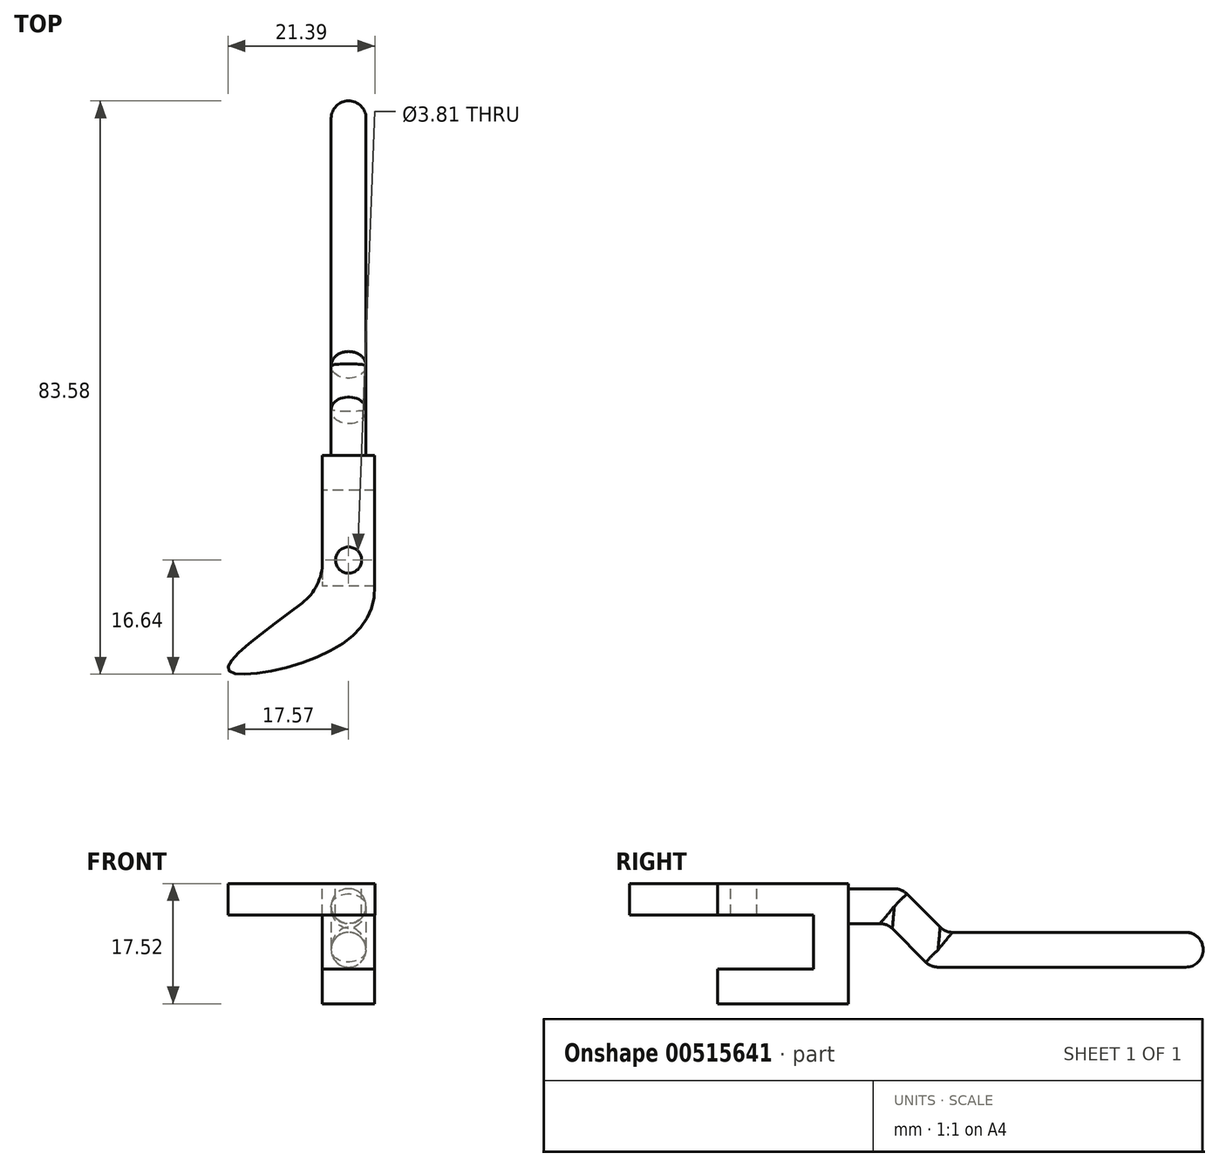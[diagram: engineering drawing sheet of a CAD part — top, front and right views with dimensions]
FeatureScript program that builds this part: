
annotation { "Feature Type Name" : "Feature", "Feature Type Description" : "" }
export const myFeature = defineFeature(function(context is Context, id is Id, definition is map)
    precondition{}
    {
        {
            var Q0;
            Q0=qCreatedBy(makeId("Top.planeOp"),FACE);
            var sketch = newSketch(context, id + "F0", { "sketchPlane" : qUnion([Q0])});
            skFitSpline(sketch, "E0", {"points": [v(0, 0) * mm, v(-13.76, -12) * mm, v(0, -9.98) * mm, v(7.62, 0) * mm], "startDerivative": vector(-32.16, -29.94) * mm, "endDerivative": vector(-1.47, 42.28) * mm});
            skLineSegment(sketch, "E1.left", {"start": v(0, 0) * mm, "end": v(0, 0) * mm});
            skLineSegment(sketch, "E1.right", {"start": v(7.62, 0) * mm, "end": v(7.62, 0) * mm});
            skLineSegment(sketch, "E2", {"start": v(7.62, 0) * mm, "end": v(7.62, 19.05) * mm});
            skLineSegment(sketch, "E3", {"start": v(7.62, 19.05) * mm, "end": v(0, 19.05) * mm});
            skLineSegment(sketch, "E4", {"start": v(0, 19.05) * mm, "end": v(0, 0) * mm});
            skSolve(sketch);
        }
        {
            var Q0;
            Q0=qSketchRegion(id+"F0",true);
            extrude(context, id + "F1", {"entities" : qUnion([Q0]), "depth" : 4.57 * mm, "offsetDistance" : 25.4 * mm});
        }
        {
            var Q0;
            Q0=makeQuery(id+"F1.opExtrude","CAP_FACE",FACE,{"disambiguationData":[OSD([sQuery(id+"F0.wireOp",EDGE,"E0"),sQuery(id+"F0.wireOp",EDGE,"E2"),sQuery(id+"F0.wireOp",EDGE,"E3"),sQuery(id+"F0.wireOp",EDGE,"E4")])],"isStart":false});
            var sketch = newSketch(context, id + "F2", { "sketchPlane" : qUnion([Q0])});
            skPoint(sketch, "E5", {"position": v(3.81, 3.81) * mm});
            skSolve(sketch);
        }
        {
            var Q0;
            Q0=sQuery(id+"F2.wireOp",VERTEX,"E5");
            var Q1;
            Q1=makeQuery(id+"F1.opExtrude","SWEPT_BODY",BODY,{"disambiguationData":[OSD([sQuery(id+"F0.wireOp",EDGE,"E0"),sQuery(id+"F0.wireOp",EDGE,"E2"),sQuery(id+"F0.wireOp",EDGE,"E3"),sQuery(id+"F0.wireOp",EDGE,"E4")])]});
            hole(context, id + "F3", {"style" : HoleStyle.SIMPLE, "endStyle" : HoleEndStyle.THROUGH, "holeDiameter" : 3.8 * mm, "isTappedThrough" : true, "tappedDepth" : 12.7 * mm, "tapClearance" : 3, "locations" : qUnion([Q0]), "scope" : qUnion([Q1])});
        }
        {
            var Q0;
            Q0=makeQuery(id+"F1.opExtrude","SWEPT_FACE",FACE,{"disambiguationData":[OSD([sQuery(id+"F0.wireOp",EDGE,"E3")])]});
            var sketch = newSketch(context, id + "F4", { "sketchPlane" : qUnion([Q0])});
            skCircle(sketch, "E6", {"center": v(-3.81, 1.27) * mm, "radius": 2.54 * mm});
            skSolve(sketch);
        }
        {
            var Q0;
            Q0 = qSketchRegion(id + "F4", true);
            extrude(context, id + "F5", {"entities" : qUnion([Q0]), "operationType" : NewBodyOperationType.ADD, "depth" : 2.54 * mm, "offsetDistance" : 25.4 * mm});
        }
        {
            var Q0;
            Q0=qCreatedBy(makeId("Right.planeOp"),FACE);
            cPlane(context, id + "F6", {"entities" : qUnion([Q0]), "cplaneType" : CPlaneType.OFFSET, "offset" : 3.8 * mm, "width" : 152.4 * mm, "height" : 152.4 * mm});
        }
        {
            var Q0;
            Q0=qCreatedBy(id+"F6.planeOp",FACE);
            var sketch = newSketch(context, id + "F7", { "sketchPlane" : qUnion([Q0])});
            skPoint(sketch, "E7", {"position": v(15.84, 2.54) * mm});
            skLineSegment(sketch, "E8", {"start": v(15.84, 2.54) * mm, "end": v(26.3, 2.54) * mm});
            skLineSegment(sketch, "E9", {"start": v(26.3, 2.54) * mm, "end": v(32.65, -3.8) * mm});
            skLineSegment(sketch, "E10", {"start": v(32.65, -3.81) * mm, "end": v(70.75, -3.81) * mm});
            skSolve(sketch);
        }
        {
            var Q0;
            Q0 = qSketchRegion(id + "F7", true);
            var Q1;
            Q1=makeQuery(id+"F5.opExtrude","CAP_FACE",FACE,{"disambiguationData":[OSD([sQuery(id+"F4.wireOp",EDGE,"E6")])],"isStart":false});
            var Q2;
            Q2=sQuery(id+"F7.wireOp",EDGE,"E8");
            var Q3;
            Q3=sQuery(id+"F7.wireOp",EDGE,"E9");
            var Q4;
            Q4=sQuery(id+"F7.wireOp",EDGE,"E10");
            sweep(context, id + "F8", {"operationType" : NewBodyOperationType.ADD, "profiles" : qUnion([Q0, Q1]), "path" : qUnion([Q2, Q3, Q4])});
        }
        {
            var Q0;
            Q0=makeQuery(id+"F8.opSweep","MID_CAP_EDGE",EDGE,{"disambiguationData":[OSD([sQuery(id+"F4.wireOp",EDGE,"E6"),sQuery(id+"F7.wireOp",VERTEX,"E10.start")])],"capPos":2.0});
            var Q1;
            Q1=makeQuery(id+"F8.opSweep","CAP_EDGE",EDGE,{"disambiguationData":[OSD([sQuery(id+"F4.wireOp",EDGE,"E6"),sQuery(id+"F7.wireOp",VERTEX,"E10.end")])],"isStart":false});
            var Q2;
            Q2=makeQuery(id+"F8.opSweep","MID_CAP_EDGE",EDGE,{"disambiguationData":[OSD([sQuery(id+"F4.wireOp",EDGE,"E6"),sQuery(id+"F7.wireOp",VERTEX,"E9.start")])],"capPos":1.0});
            var Q3;
            {var subQ0=sQuery(id+"F0.wireOp",EDGE,"E3");var subQ1=sQuery(id+"F4.wireOp",EDGE,"E6");var subQ2=makeQuery(id+"F5.opExtrude","SWEPT_FACE",FACE,{"disambiguationData":[OSD([subQ1])]});var subQ3=makeQuery(id+"F5.opExtrude","CAP_FACE",FACE,{"disambiguationData":[OSD([subQ1])],"isStart":true});Q3=makeQuery(id+"F5.boolean.opBoolean","SPLIT",EDGE,{"disambiguationData":[topologyDisambiguationEdgeConnected([subQ2,subQ3]),TD([makeQuery(id+"F1.opExtrude","CAP_FACE",FACE,{"disambiguationData":[OSD([sQuery(id+"F0.wireOp",EDGE,"E0"),sQuery(id+"F0.wireOp",EDGE,"E2"),subQ0,sQuery(id+"F0.wireOp",EDGE,"E4")])],"isStart":false})])],"derivedFrom":makeQuery(id+"F5.opExtrude","CAP_EDGE",EDGE,{"disambiguationData":[OSD([subQ1])],"isStart":true})});}
            fillet(context, id + "F9", {"entities" : qUnion([Q0, Q1, Q2, Q3]), "radius" : 2.54 * mm, "tangentPropagation" : true, "allowEdgeOverflow" : false});
        }
        {
            var Q0;
            Q0=makeQuery(id+"F1.opExtrude","CAP_FACE",FACE,{"disambiguationData":[OSD([sQuery(id+"F0.wireOp",EDGE,"E0"),sQuery(id+"F0.wireOp",EDGE,"E2"),sQuery(id+"F0.wireOp",EDGE,"E3"),sQuery(id+"F0.wireOp",EDGE,"E4")])],"isStart":true});
            var sketch = newSketch(context, id + "F10", { "sketchPlane" : qUnion([Q0])});
            skLineSegment(sketch, "E11.bottom", {"start": v(7.62, -19.05) * mm, "end": v(0, -19.05) * mm});
            skLineSegment(sketch, "E11.top", {"start": v(7.62, -13.97) * mm, "end": v(0, -13.97) * mm});
            skLineSegment(sketch, "E11.left", {"start": v(7.62, -19.05) * mm, "end": v(7.62, -13.97) * mm});
            skLineSegment(sketch, "E11.right", {"start": v(0, -19.05) * mm, "end": v(0, -13.97) * mm});
            skSolve(sketch);
        }
        {
            var Q0;
            Q0 = qSketchRegion(id + "F10", true);
            extrude(context, id + "F11", {"entities" : qUnion([Q0]), "operationType" : NewBodyOperationType.ADD, "depth" : 7.87 * mm, "offsetDistance" : 25.4 * mm});
        }
        {
            var Q0;
            Q0=makeQuery(id+"F11.opExtrude","CAP_FACE",FACE,{"disambiguationData":[OSD([sQuery(id+"F10.wireOp",EDGE,"E11.bottom"),sQuery(id+"F10.wireOp",EDGE,"E11.top"),sQuery(id+"F10.wireOp",EDGE,"E11.left"),sQuery(id+"F10.wireOp",EDGE,"E11.right")])],"isStart":false});
            var sketch = newSketch(context, id + "F12", { "sketchPlane" : qUnion([Q0])});
            skLineSegment(sketch, "E12.bottom", {"start": v(7.62, -19.05) * mm, "end": v(0, -19.05) * mm});
            skLineSegment(sketch, "E12.top", {"start": v(7.62, 0) * mm, "end": v(0, 0) * mm});
            skLineSegment(sketch, "E12.left", {"start": v(7.62, -19.05) * mm, "end": v(7.62, 0) * mm});
            skLineSegment(sketch, "E12.right", {"start": v(0, -19.05) * mm, "end": v(0, 0) * mm});
            skSolve(sketch);
        }
        {
            var Q0;
            Q0 = qSketchRegion(id + "F12", true);
            extrude(context, id + "F13", {"entities" : qUnion([Q0]), "operationType" : NewBodyOperationType.ADD, "depth" : 5.08 * mm, "offsetDistance" : 25.4 * mm});
        }
        {
            var Q0;
            Q0=makeQuery(id+"F1.opExtrude","SWEPT_EDGE",EDGE,{"disambiguationData":[OSD([sQuery(id+"F0.wireOp",EDGE,"E0"),sQuery(id+"F0.wireOp",EDGE,"E4")])]});
            fillet(context, id + "F14", {"entities" : qUnion([Q0]), "radius" : 7.62 * mm, "tangentPropagation" : true, "allowEdgeOverflow" : false});
        }
    });
